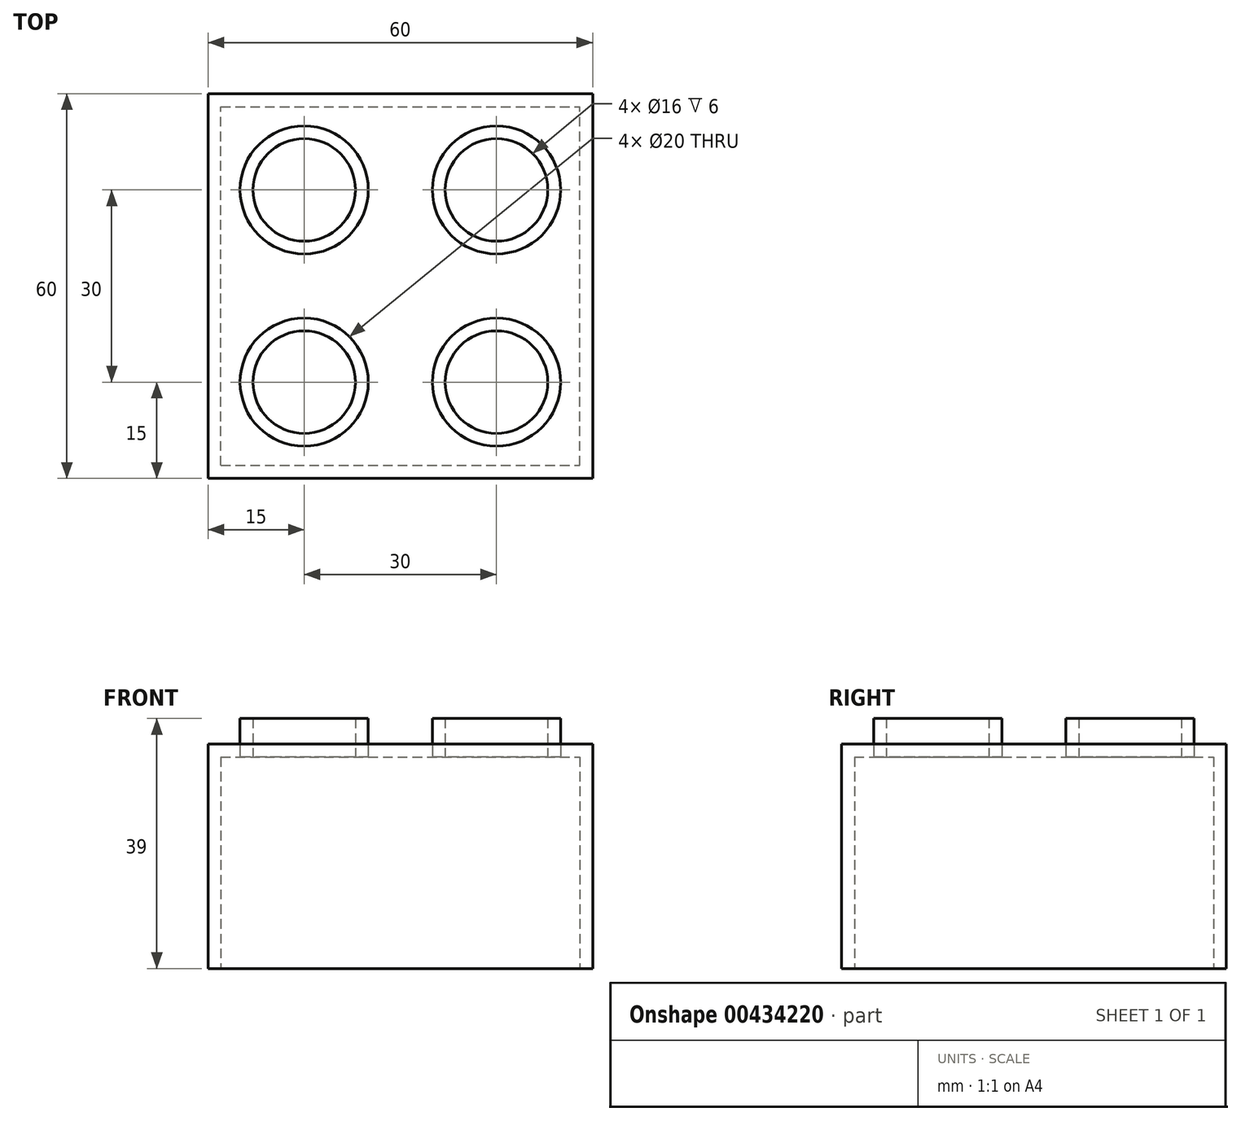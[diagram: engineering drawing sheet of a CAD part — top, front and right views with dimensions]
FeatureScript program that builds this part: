
annotation { "Feature Type Name" : "Feature", "Feature Type Description" : "" }
export const myFeature = defineFeature(function(context is Context, id is Id, definition is map)
    precondition{}
    {
        {
            var Q0;
            Q0=qCreatedBy(makeId("Top.planeOp"),FACE);
            var sketch = newSketch(context, id + "F0", { "sketchPlane" : qUnion([Q0])});
            skLineSegment(sketch, "E0.bottom", {"start": v(0, 0) * mm, "end": v(60, 0) * mm});
            skLineSegment(sketch, "E0.top", {"start": v(0, -60) * mm, "end": v(60, -60) * mm});
            skLineSegment(sketch, "E0.left", {"start": v(0, 0) * mm, "end": v(0, -60) * mm});
            skLineSegment(sketch, "E0.right", {"start": v(60, 0) * mm, "end": v(60, -60) * mm});
            skLineSegment(sketch, "E1", {"start": v(60, -60) * mm, "end": v(60, -45) * mm});
            skLineSegment(sketch, "E2", {"start": v(60, -60) * mm, "end": v(45, -60) * mm});
            skLineSegment(sketch, "E3", {"start": v(0, -60) * mm, "end": v(15, -60) * mm});
            skLineSegment(sketch, "E4", {"start": v(0, -60) * mm, "end": v(0, -45) * mm});
            skLineSegment(sketch, "E5", {"start": v(0, 0) * mm, "end": v(0, -15) * mm});
            skLineSegment(sketch, "E6", {"start": v(0, 0) * mm, "end": v(15, 0) * mm});
            skLineSegment(sketch, "E7", {"start": v(60, 0) * mm, "end": v(45, 0) * mm});
            skLineSegment(sketch, "E8", {"start": v(60, 0) * mm, "end": v(60, -8.63) * mm});
            skLineSegment(sketch, "E9", {"start": v(45, -60) * mm, "end": v(45, -45) * mm});
            skLineSegment(sketch, "E10", {"start": v(15, -60) * mm, "end": v(15, -45) * mm});
            skLineSegment(sketch, "E11", {"start": v(0, -15) * mm, "end": v(15, -15) * mm});
            skLineSegment(sketch, "E12", {"start": v(45, 0) * mm, "end": v(45, -15) * mm});
            skCircle(sketch, "E13", {"center": v(15, -15) * mm, "radius": 10 * mm});
            skCircle(sketch, "E14", {"center": v(15, -45) * mm, "radius": 10 * mm});
            skCircle(sketch, "E15", {"center": v(45, -45) * mm, "radius": 10 * mm});
            skCircle(sketch, "E16", {"center": v(45, -15) * mm, "radius": 10 * mm});
            skCircle(sketch, "E17", {"center": v(15, -15) * mm, "radius": 8 * mm});
            skCircle(sketch, "E18", {"center": v(45, -15) * mm, "radius": 8 * mm});
            skCircle(sketch, "E19", {"center": v(45, -45) * mm, "radius": 8 * mm});
            skCircle(sketch, "E20", {"center": v(15, -45) * mm, "radius": 8 * mm});
            skSolve(sketch);
        }
        {
            var Q0;
            Q0=makeQuery(id+"F0.imprint","IMPRINT",FACE,{"disambiguationData":[TD([[makeQuery(id+"F0.imprint","IMPRINT",EDGE,{"derivedFrom":sQuery(id+"F0.wireOp",EDGE,"E16")}),1.0]])]});
            var Q1;
            Q1=makeQuery(id+"F0.imprint","IMPRINT",FACE,{"disambiguationData":[TD([[makeQuery(id+"F0.imprint","IMPRINT",EDGE,{"derivedFrom":sQuery(id+"F0.wireOp",EDGE,"E13")}),1.0]])]});
            var Q2;
            Q2=makeQuery(id+"F0.imprint","IMPRINT",FACE,{"disambiguationData":[TD([[makeQuery(id+"F0.imprint","IMPRINT",EDGE,{"derivedFrom":sQuery(id+"F0.wireOp",EDGE,"E14")}),1.0]])]});
            var Q3;
            Q3=makeQuery(id+"F0.imprint","IMPRINT",FACE,{"disambiguationData":[TD([[makeQuery(id+"F0.imprint","IMPRINT",EDGE,{"derivedFrom":sQuery(id+"F0.wireOp",EDGE,"E15")}),1.0]])]});
            extrude(context, id + "F1", {"entities" : qUnion([Q0, Q1, Q2, Q3]), "depth" : 39 * mm});
        }
        {
            var Q0;
            Q0=makeQuery(id+"F0.imprint","IMPRINT",FACE,{"disambiguationData":[TD([[makeQuery(id+"F0.imprint","IMPRINT",EDGE,{"derivedFrom":sQuery(id+"F0.wireOp",EDGE,"E0.bottom")}),-1.0]])]});
            extrude(context, id + "F2", {"entities" : qUnion([Q0]), "depth" : 35 * mm});
        }
        {
            var Q0;
            Q0=qCreatedBy(makeId("Top.planeOp"),FACE);
            var sketch = newSketch(context, id + "F3", { "sketchPlane" : qUnion([Q0])});
            skLineSegment(sketch, "E21", {"start": v(0, 0) * mm, "end": v(0, -30) * mm});
            skLineSegment(sketch, "E22", {"start": v(0, -30) * mm, "end": v(30, -30) * mm});
            skLineSegment(sketch, "E23.bottom", {"start": v(2, -58) * mm, "end": v(58, -58) * mm});
            skLineSegment(sketch, "E23.top", {"start": v(2, -2) * mm, "end": v(58, -2) * mm});
            skLineSegment(sketch, "E23.left", {"start": v(2, -58) * mm, "end": v(2, -2) * mm});
            skLineSegment(sketch, "E23.right", {"start": v(58, -58) * mm, "end": v(58, -2) * mm});
            skPoint(sketch, "E23.middle", {"position": v(30, -30) * mm});
            skSolve(sketch);
        }
        {
            var Q0;
            {var subQ0=sQuery(id+"F3.wireOp",EDGE,"E23.bottom");Q0=makeQuery(id+"F3.imprint","IMPRINT",FACE,{"disambiguationData":[TD([[makeQuery(id+"F3.imprint","IMPRINT",EDGE,{"derivedFrom":subQ0}),1.0]])]});}
            extrude(context, id + "F4", {"entities" : qUnion([Q0]), "operationType" : NewBodyOperationType.REMOVE, "depth" : 33 * mm});
        }
    });
